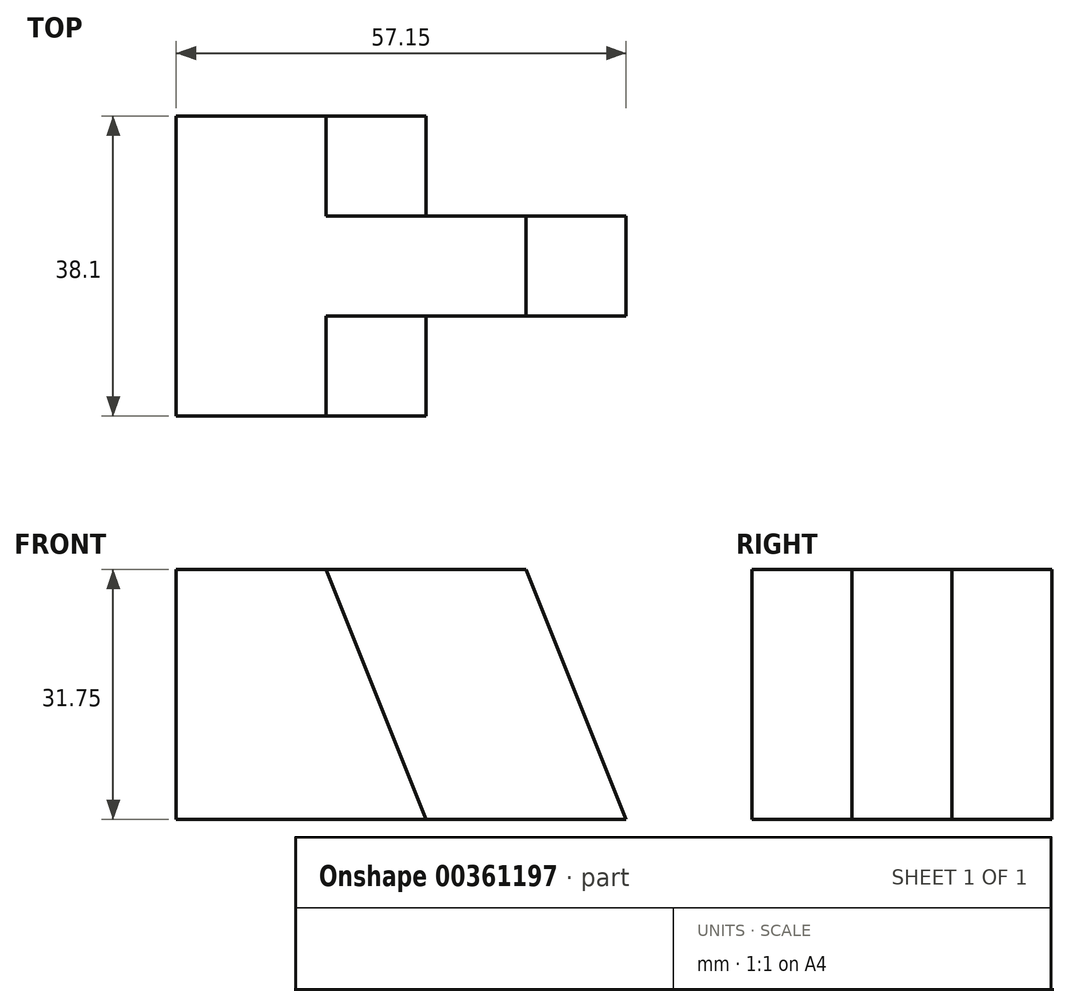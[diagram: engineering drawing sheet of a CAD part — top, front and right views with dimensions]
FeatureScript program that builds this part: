
annotation { "Feature Type Name" : "Feature", "Feature Type Description" : "" }
export const myFeature = defineFeature(function(context is Context, id is Id, definition is map)
    precondition{}
    {
        {
            var Q0;
            Q0=qCreatedBy(makeId("Top.planeOp"),FACE);
            var sketch = newSketch(context, id + "F0", { "sketchPlane" : qUnion([Q0])});
            skLineSegment(sketch, "E0", {"start": v(0, 0) * mm, "end": v(0, 38.1) * mm});
            skLineSegment(sketch, "E1", {"start": v(0, 38.1) * mm, "end": v(31.75, 38.1) * mm});
            skLineSegment(sketch, "E2", {"start": v(31.75, 38.1) * mm, "end": v(31.75, 25.4) * mm});
            skLineSegment(sketch, "E3", {"start": v(31.75, 25.4) * mm, "end": v(57.15, 25.4) * mm});
            skLineSegment(sketch, "E4", {"start": v(57.15, 25.4) * mm, "end": v(57.15, 12.7) * mm});
            skLineSegment(sketch, "E5", {"start": v(57.15, 12.7) * mm, "end": v(31.75, 12.7) * mm});
            skLineSegment(sketch, "E6", {"start": v(31.75, 12.7) * mm, "end": v(31.75, 0) * mm});
            skLineSegment(sketch, "E7", {"start": v(31.75, 0) * mm, "end": v(0, 0) * mm});
            skSolve(sketch);
        }
        {
            var Q0;
            Q0 = qSketchRegion(id + "F0", true);
            extrude(context, id + "F1", {"entities" : qUnion([Q0]), "depth" : 31.75 * mm});
        }
        {
            var Q0;
            Q0=makeQuery(id+"F1.opExtrude","SWEPT_FACE",FACE,{"disambiguationData":[OSD([sQuery(id+"F0.wireOp",EDGE,"E7")])]});
            var sketch = newSketch(context, id + "F2", { "sketchPlane" : qUnion([Q0])});
            skLineSegment(sketch, "E8", {"start": v(19.05, 31.75) * mm, "end": v(31.75, 0) * mm});
            skLineSegment(sketch, "E9", {"start": v(31.75, 0) * mm, "end": v(31.75, 31.75) * mm});
            skLineSegment(sketch, "E10", {"start": v(31.75, 31.75) * mm, "end": v(19.05, 31.75) * mm});
            skSolve(sketch);
        }
        {
            var Q0;
            Q0 = qSketchRegion(id + "F2", true);
            extrude(context, id + "F3", {"entities" : qUnion([Q0]), "operationType" : NewBodyOperationType.REMOVE, "oppositeDirection" : true, "depth" : 12.7 * mm});
        }
        {
            var Q0;
            Q0=makeQuery(id+"F3.boolean.opBoolean","MERGE",FACE,{"derivedFrom":[makeQuery(id+"F1.opExtrude","SWEPT_FACE",FACE,{"disambiguationData":[OSD([sQuery(id+"F0.wireOp",EDGE,"E5")])]}),makeQuery(id+"F3.opExtrude","CAP_FACE",FACE,{"disambiguationData":[OSD([sQuery(id+"F2.wireOp",EDGE,"E8"),sQuery(id+"F2.wireOp",EDGE,"E9"),sQuery(id+"F2.wireOp",EDGE,"E10")])],"isStart":false})]});
            var sketch = newSketch(context, id + "F4", { "sketchPlane" : qUnion([Q0])});
            skLineSegment(sketch, "E11", {"start": v(44.45, 31.75) * mm, "end": v(57.15, 0) * mm});
            skLineSegment(sketch, "E12", {"start": v(57.15, 0) * mm, "end": v(57.15, 31.75) * mm});
            skLineSegment(sketch, "E13", {"start": v(57.15, 31.75) * mm, "end": v(44.45, 31.75) * mm});
            skSolve(sketch);
        }
        {
            var Q0;
            Q0 = qSketchRegion(id + "F4", true);
            extrude(context, id + "F5", {"entities" : qUnion([Q0]), "operationType" : NewBodyOperationType.REMOVE, "oppositeDirection" : true, "depth" : 12.7 * mm});
        }
        {
            var Q0;
            Q0=makeQuery(id+"F1.opExtrude","SWEPT_FACE",FACE,{"disambiguationData":[OSD([sQuery(id+"F0.wireOp",EDGE,"E1")])]});
            var sketch = newSketch(context, id + "F6", { "sketchPlane" : qUnion([Q0])});
            skLineSegment(sketch, "E14", {"start": v(-19.05, 31.75) * mm, "end": v(-31.75, 0) * mm});
            skLineSegment(sketch, "E15", {"start": v(-31.75, 0) * mm, "end": v(-31.75, 31.75) * mm});
            skLineSegment(sketch, "E16", {"start": v(-31.75, 31.75) * mm, "end": v(-19.05, 31.75) * mm});
            skSolve(sketch);
        }
        {
            var Q0;
            Q0 = qSketchRegion(id + "F6", true);
            extrude(context, id + "F7", {"entities" : qUnion([Q0]), "operationType" : NewBodyOperationType.REMOVE, "oppositeDirection" : true, "depth" : 12.7 * mm});
        }
        {
            var Q0;
            Q0 = qSketchRegion(id + "F4", true);
            extrude(context, id + "F8", {"entities" : qUnion([Q0]), "operationType" : NewBodyOperationType.REMOVE, "oppositeDirection" : true, "depth" : 25.4 * mm});
        }
    });
